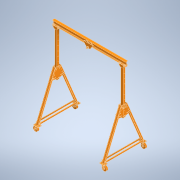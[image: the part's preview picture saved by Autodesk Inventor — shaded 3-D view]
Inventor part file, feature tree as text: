
AUTODESK INVENTOR PART (.ipt)
format: ipt  version: 2022 (Build 260153000, 153)  size: 9,937,408 bytes
history: native  units: in
note: dims shown in document units (in); Inventor stores cm internally (conversion verified against a paired STEP export)
features: other x162, mirror x63, chamfer x2, revolve x2, sweep x1, boolean_combine x1
ambient origin geometry x8: Origin, YZ Plane, XZ Plane, XY Plane, X Axis, Y Axis, Z Axis, Center Point
bodies: Solid1 (feature_tree), Solid2 (feature_tree), Solid3 (feature_tree), Solid4 (feature_tree), Solid5 (feature_tree), Solid6 (feature_tree), Solid7 (feature_tree), Solid8 (feature_tree), Solid9 (feature_tree), Solid10 (feature_tree), Solid11 (feature_tree), Solid12 (feature_tree), Solid13 (feature_tree), Solid14 (feature_tree), Solid15 (feature_tree), Solid16 (feature_tree), Solid17 (feature_tree), Solid18 (feature_tree), Solid19 (feature_tree), Solid20 (feature_tree), Solid21 (feature_tree), Solid22 (feature_tree), Solid23 (feature_tree), Solid24 (feature_tree), Solid25 (feature_tree), Solid26 (feature_tree), Solid27 (feature_tree), Solid28 (feature_tree), Solid29 (feature_tree), Solid30 (feature_tree), Solid31 (feature_tree), Solid32 (feature_tree), Solid33 (feature_tree), Solid34 (feature_tree), Solid35 (feature_tree), Solid36 (feature_tree), Solid37 (feature_tree), Solid38 (feature_tree), Solid39 (feature_tree), Solid40 (feature_tree), Solid41 (feature_tree), Solid42 (feature_tree), Solid43 (feature_tree), Solid44 (feature_tree), Solid45 (feature_tree), Solid46 (feature_tree), Solid47 (feature_tree), Solid48 (feature_tree), Solid49 (feature_tree), Solid50 (feature_tree), Solid51 (feature_tree), Solid52 (feature_tree), Solid53 (feature_tree), Solid54 (feature_tree), Solid55 (feature_tree), Solid56 (feature_tree), Solid57 (feature_tree), Solid58 (feature_tree), Solid59 (feature_tree), Solid60 (feature_tree), Solid61 (feature_tree), Solid62 (feature_tree), Solid63 (feature_tree), Solid64 (feature_tree), Solid65 (feature_tree), Solid66 (feature_tree), Solid67 (feature_tree), Solid68 (feature_tree), Solid69 (feature_tree), Solid70 (feature_tree), Solid71 (feature_tree), Solid72 (feature_tree), Solid73 (feature_tree), Solid74 (feature_tree), Solid75 (feature_tree), Solid76 (feature_tree), Solid77 (feature_tree), Solid78 (feature_tree), Solid79 (feature_tree), Solid80 (feature_tree), Solid81 (feature_tree), Solid82 (feature_tree), Solid83 (feature_tree), Solid84 (feature_tree), Solid85 (feature_tree), Solid86 (feature_tree), Solid87 (feature_tree), Solid88 (feature_tree), Solid89 (feature_tree), Solid90 (feature_tree), Solid91 (feature_tree), Solid92 (feature_tree), Solid93 (feature_tree), Solid94 (feature_tree), Solid95 (feature_tree), Solid96 (feature_tree), Solid97 (feature_tree), Solid98 (feature_tree), Solid99 (feature_tree), Solid100 (feature_tree), Solid101 (feature_tree), Solid102 (feature_tree), Solid103 (feature_tree), Solid104 (feature_tree), Solid105 (feature_tree), Solid106 (feature_tree), Solid107 (feature_tree), Solid108 (feature_tree), Solid109 (feature_tree), Solid110 (feature_tree), Solid111 (feature_tree), Solid112 (feature_tree), Solid113 (feature_tree), Solid114 (feature_tree), Solid115 (feature_tree), Solid116 (feature_tree), Solid117 (feature_tree), Solid118 (feature_tree), Solid119 (feature_tree), Solid120 (feature_tree), Solid121 (feature_tree), Solid122 (feature_tree), Solid123 (feature_tree), Solid124 (feature_tree), Solid125 (feature_tree), Solid126 (feature_tree), Solid127 (feature_tree), Solid128 (feature_tree), Solid129 (feature_tree), Solid130 (feature_tree), Solid131 (feature_tree), Solid132 (feature_tree), Solid133 (feature_tree), Solid134 (feature_tree), Solid135 (feature_tree), Solid136 (feature_tree), Solid137 (feature_tree), Solid138 (feature_tree), Solid139 (feature_tree), Solid140 (feature_tree), Solid141 (feature_tree), Solid142 (feature_tree), Solid143 (feature_tree), Solid144 (feature_tree), Solid145 (feature_tree), Solid146 (feature_tree), Solid147 (feature_tree), Solid148 (feature_tree), Solid149 (feature_tree), Solid150 (feature_tree), Solid151 (feature_tree), Solid152 (feature_tree), Solid153 (feature_tree), Solid154 (feature_tree), Solid155 (feature_tree), Solid156 (feature_tree), Solid157 (feature_tree), Solid158 (feature_tree), Solid159 (feature_tree), Solid160 (feature_tree), Solid161 (feature_tree), Solid162 (feature_tree), Solid163 (feature_tree), Solid164 (feature_tree), Solid165 (feature_tree), Solid166 (feature_tree), Solid167 (feature_tree), Solid168 (feature_tree), Solid169 (feature_tree), Solid170 (feature_tree), Solid171 (feature_tree), Solid172 (feature_tree), Solid173 (feature_tree), Solid174 (feature_tree), Solid175 (feature_tree), Solid176 (feature_tree), Solid177 (feature_tree), Solid178 (feature_tree), Solid179 (feature_tree), Solid180 (feature_tree), Solid181 (feature_tree), Solid182 (feature_tree), Solid183 (feature_tree), Solid184 (feature_tree), Solid185 (feature_tree), Solid186 (feature_tree), Solid187 (feature_tree), Solid188 (feature_tree), Solid189 (feature_tree), Solid190 (feature_tree), Solid191 (feature_tree), Solid192 (feature_tree), Solid193 (feature_tree), Solid194 (feature_tree), Solid195 (feature_tree), Solid196 (feature_tree), Solid197 (feature_tree), Solid198 (feature_tree), Solid199 (feature_tree), Solid200 (feature_tree), Solid201 (feature_tree), Solid202 (feature_tree), Solid203 (feature_tree), Solid204 (feature_tree), Solid205 (feature_tree), Solid206 (feature_tree), Solid207 (feature_tree), Solid208 (feature_tree), Solid209 (feature_tree), Solid210 (feature_tree), Solid211 (feature_tree), Solid212 (feature_tree), Solid213 (feature_tree), Solid214 (feature_tree), Solid215 (feature_tree), Solid216 (feature_tree), Solid217 (feature_tree), Solid218 (feature_tree), Solid219 (feature_tree), Solid220 (feature_tree), Solid221 (feature_tree), Solid222 (feature_tree), Solid223 (feature_tree), Solid224 (feature_tree), Solid225 (feature_tree), Solid226 (feature_tree), Solid227 (feature_tree), Solid228 (feature_tree), Solid229 (feature_tree), Solid230 (feature_tree), Solid231 (feature_tree)
feature tree (231):
  other  "Boss-Extrude2"
  sweep  "Sweep1"
  chamfer  "Chamfer1"  [1 undecoded]
  other  "LPattern1[1]"
  other  "LPattern1[2]"
  other  "LPattern1[3]"
  mirror  "Mirror2"
  other  "LPattern3[1]"
  other  "LPattern3[2]"
  other  "LPattern3[3]"
  other  "LPattern3[4]"
  other  "LPattern3[5]"
  other  "LPattern3[6]"
  mirror  "Mirror3[1]"
  mirror  "Mirror3[2]"
  mirror  "Mirror3[3]"
  mirror  "Mirror3[4]"
  mirror  "Mirror3[5]"
  mirror  "Mirror3[6]"
  mirror  "Mirror3[7]"
  mirror  "Mirror3[8]"
  mirror  "Mirror3[9]"
  mirror  "Mirror3[10]"
  mirror  "Mirror3[11]"
  mirror  "Mirror3[12]"
  mirror  "Mirror4[1]"
  mirror  "Mirror4[2]"
  mirror  "Mirror4[3]"
  mirror  "Mirror4[4]"
  mirror  "Mirror4[5]"
  mirror  "Mirror4[6]"
  mirror  "Mirror4[7]"
  mirror  "Mirror4[8]"
  mirror  "Mirror4[9]"
  mirror  "Mirror4[10]"
  mirror  "Mirror4[11]"
  mirror  "Mirror4[12]"
  mirror  "Mirror4[13]"
  mirror  "Mirror4[14]"
  mirror  "Mirror4[15]"
  mirror  "Mirror4[16]"
  mirror  "Mirror4[17]"
  mirror  "Mirror4[18]"
  mirror  "Mirror4[19]"
  mirror  "Mirror4[20]"
  mirror  "Mirror4[21]"
  mirror  "Mirror4[22]"
  mirror  "Mirror4[23]"
  mirror  "Mirror4[24]"
  other  "Cut-Extrude3"
  mirror  "Mirror4[25]"
  mirror  "Mirror5[1]"
  mirror  "Mirror4[26]"
  other  "Boss-Extrude6"
  mirror  "Mirror6"
  chamfer  "Chamfer2"  [1 undecoded]
  mirror  "Mirror5[2]"
  mirror  "Mirror4[27]"
  mirror  "Mirror4[28]"
  mirror  "Mirror4[29]"
  mirror  "Mirror4[30]"
  revolve  "Revolve1"  [1 undecoded]
  revolve  "Revolve3"  [1 undecoded]
  other  "LPattern4[1]"
  other  "LPattern4[2]"
  other  "LPattern4[3]"
  other  "LPattern4[4]"
  other  "LPattern4[5]"
  other  "LPattern4[6]"
  other  "LPattern4[7]"
  mirror  "Mirror7"
  other  "LPattern5[1]"
  other  "LPattern5[2]"
  mirror  "Mirror8"
  mirror  "Mirror9"
  mirror  "Mirror10[1]"
  mirror  "Mirror10[2]"
  mirror  "Mirror10[3]"
  mirror  "Mirror10[5]"
  mirror  "Mirror10[6]"
  mirror  "Mirror10[7]"
  mirror  "Mirror10[8]"
  mirror  "Mirror10[9]"
  mirror  "Mirror10[10]"
  mirror  "Mirror10[11]"
  mirror  "Mirror10[12]"
  mirror  "Mirror10[13]"
  mirror  "Mirror10[14]"
  mirror  "Mirror10[15]"
  boolean_combine  "Combine2"
  other  "Boss-Extrude15"
  other  "1a[1]"
  other  "1a[2]"
  other  "1a[3]"
  other  "1a[4]"
  other  "1a[5]"
  other  "1a[6]"
  other  "1a[7]"
  other  "1a[8]"
  other  "1a[9]"
  other  "1a[10]"
  other  "1a[11]"
  other  "1a[12]"
  other  "1a[13]"
  other  "1a[14]"
  other  "1a[15]"
  other  "1a[16]"
  other  "1a[17]"
  other  "1a[18]"
  other  "1a[19]"
  other  "1a[20]"
  other  "1a[21]"
  other  "1a[22]"
  other  "1a[23]"
  other  "1a[24]"
  other  "1a[25]"
  other  "1a[26]"
  other  "1a[27]"
  other  "1a[28]"
  other  "1a[29]"
  other  "1a[30]"
  other  "1a[31]"
  other  "1a[32]"
  other  "1a[33]"
  other  "1a[34]"
  other  "1a[35]"
  other  "1a[36]"
  other  "1a[37]"
  other  "1a[38]"
  other  "1a[39]"
  other  "1a[40]"
  other  "1a[41]"
  other  "1a[42]"
  other  "1a[43]"
  other  "1a[44]"
  other  "1a[45]"
  other  "1a[46]"
  other  "1a[47]"
  other  "1a[48]"
  other  "1a[49]"
  other  "1a[50]"
  other  "1a[51]"
  other  "1a[52]"
  other  "1a[53]"
  other  "1a[54]"
  other  "1a[55]"
  other  "1a[56]"
  other  "1a[57]"
  other  "1a[58]"
  other  "1a[59]"
  other  "1a[60]"
  other  "1a[61]"
  other  "1a[62]"
  other  "1a[63]"
  other  "1a[64]"
  other  "1a[65]"
  other  "1a[66]"
  other  "1a[67]"
  other  "1a[68]"
  other  "1a[69]"
  other  "1a[70]"
  other  "1c[1]"
  other  "1c[2]"
  other  "1c[3]"
  other  "1c[4]"
  other  "1c[5]"
  other  "1c[6]"
  other  "1c[7]"
  other  "1c[8]"
  other  "1c[9]"
  other  "1c[10]"
  other  "1c[11]"
  other  "1c[12]"
  other  "1c[13]"
  other  "1c[14]"
  other  "1c[15]"
  other  "1c[16]"
  other  "1c[17]"
  other  "1c[18]"
  other  "1c[19]"
  other  "1c[20]"
  other  "1c[21]"
  other  "1c[22]"
  other  "1c[23]"
  other  "1c[24]"
  other  "1c[25]"
  other  "1c[26]"
  other  "1c[27]"
  other  "1c[28]"
  other  "1c[29]"
  other  "1c[30]"
  other  "1c[31]"
  other  "1c[32]"
  other  "1c[33]"
  other  "1c[34]"
  other  "1c[35]"
  other  "1c[36]"
  other  "1c[37]"
  other  "1c[38]"
  other  "1c[39]"
  other  "1c[40]"
  other  "1c[41]"
  other  "1c[42]"
  other  "1c[43]"
  other  "1c[44]"
  other  "1c[45]"
  other  "1c[46]"
  other  "1c[47]"
  other  "1c[48]"
  other  "1c[49]"
  other  "1c[50]"
  other  "1c[51]"
  other  "1c[52]"
  other  "1c[53]"
  other  "1c[54]"
  other  "1c[55]"
  other  "1c[56]"
  other  "1c[57]"
  other  "1c[58]"
  other  "1c[59]"
  other  "1c[60]"
  other  "1c[61]"
  other  "1c[62]"
  other  "1c[63]"
  other  "1c[64]"
  other  "1c[65]"
  other  "1c[66]"
  other  "1c[67]"
  other  "1c[68]"
  other  "1c[69]"
  other  "1c[70]"
note: 4 required parameter values undecoded (feature->parameter linkage not recoverable at this tier; creation-order binding heuristic only, values carry confidence <= 0.55)
